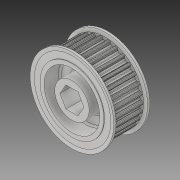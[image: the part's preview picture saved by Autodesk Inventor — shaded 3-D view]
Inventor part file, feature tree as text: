
AUTODESK INVENTOR PART (.ipt)
format: ipt  version: 2019 (Build 230136000, 136)  size: 902,656 bytes
history: native  units: in
note: dims shown in document units (in); Inventor stores cm internally (conversion verified against a paired STEP export)
features: mirror x1
ambient origin geometry x8: Origin, YZ Plane, XZ Plane, XY Plane, X Axis, Y Axis, Z Axis, Center Point
bodies: Solid1 (feature_tree)
feature tree (1):
  mirror  "Mirror1"
